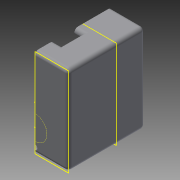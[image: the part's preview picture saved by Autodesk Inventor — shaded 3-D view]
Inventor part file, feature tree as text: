
AUTODESK INVENTOR PART (.ipt)
format: ipt  version: 2013 (Build 170138000, 138)  size: 291,840 bytes
history: native  units: in
note: dims shown in document units (in); Inventor stores cm internally (conversion verified against a paired STEP export)
features: sketch x13, other x4, plane x1
ambient origin geometry x8: Origin, YZ Plane, XZ Plane, XY Plane, X Axis, Y Axis, Z Axis, Center Point
bodies: Solid1 (feature_tree)
feature tree (18):
  other  "design.ipt"
  other  "Solid1::design.ipt"
  other  "TaggingFeature1"
  sketch  "Sketch1"  dims[d0=0.3937in]
  sketch  "Sketch2"  dims[d1=1.8701in d2=1.0106in d3=0.0in d4=0.4803in d6=0.6563in d7=0.0in d8=0.5846in d10=0.8925in d11=0.0in d12=0.5118in d13=0.2362in d14=0.0in d15=0.1181in d17=0.0787in d18=0.1181in d19=0.0in d20=45.0deg d21=0.1575in d22=0.0in d23=0.1969in d24=0.2559in d25=0.7874in d26=0.0in d27=0.5906in d28=0.1969in d29=0.4921in d30=0.0in d32=0.0197in d35=0.0591in d36=0.0in d37=0.1181in d38=0.0in d39=0.7874in d40=0.1575in d41=0.4331in d42=0.1575in d43=0.0in d44=0.0787in d45=0.0197in d46=0.0197in d47=0.0197in d48=0.0787in]
  sketch  "Sketch3"
  sketch  "Sketch4"
  sketch  "Sketch5"
  sketch  "Sketch6"
  sketch  "Sketch7"
  sketch  "Sketch11"
  sketch  "Sketch12"
  sketch  "Sketch13"
  sketch  "Sketch14"
  other  "Pin Trench"
  sketch  "Sketch16"
  sketch  "Sketch17"
  plane  "Work Plane1"
